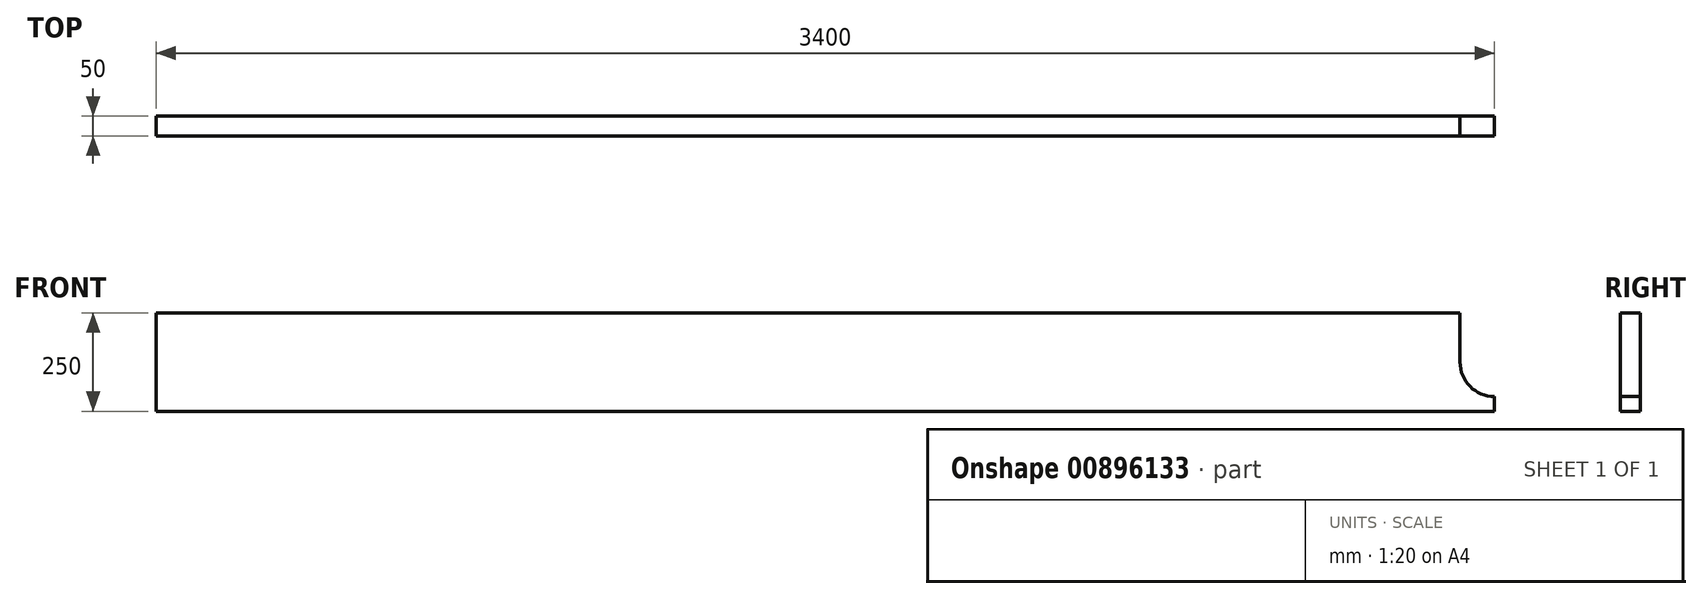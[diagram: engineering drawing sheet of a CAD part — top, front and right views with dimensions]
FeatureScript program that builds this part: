
annotation { "Feature Type Name" : "Feature", "Feature Type Description" : "" }
export const myFeature = defineFeature(function(context is Context, id is Id, definition is map)
    precondition{}
    {
        {
            var Q0;
            Q0=qCreatedBy(makeId("Front.planeOp"),FACE);
            var sketch = newSketch(context, id + "F0", { "sketchPlane" : qUnion([Q0])});
            skLineSegment(sketch, "E0.bottom", {"start": v(0, 0) * mm, "end": v(-3400, 0) * mm});
            skLineSegment(sketch, "E0.top", {"start": v(0, 250) * mm, "end": v(-3400, 250) * mm});
            skLineSegment(sketch, "E0.left", {"start": v(0, 0) * mm, "end": v(0, 250) * mm});
            skLineSegment(sketch, "E0.right", {"start": v(-3400, 0) * mm, "end": v(-3400, 250) * mm});
            skCircle(sketch, "E1", {"center": v(0, 125) * mm, "radius": 87.5 * mm});
            skLineSegment(sketch, "E2", {"start": v(-87.5, 250) * mm, "end": v(-87.5, 125) * mm});
            skSolve(sketch);
        }
        {
            var Q0;
            Q0=makeQuery(id+"F0.imprint","IMPRINT",FACE,{"disambiguationData":[TD([[makeQuery(id+"F0.imprint","IMPRINT",EDGE,{"derivedFrom":sQuery(id+"F0.wireOp",EDGE,"E0.bottom")}),-1.0]])]});
            extrude(context, id + "F1", {"entities" : qUnion([Q0]), "oppositeDirection" : true, "depth" : 50 * mm, "offsetDistance" : 25 * mm});
        }
        {
            var Q0;
            Q0=sQuery(id+"F0.wireOp",VERTEX,"E0.top.start");
            var Q1;
            Q1=makeQuery(id+"F1.opExtrude","SWEPT_BODY",BODY,{"disambiguationData":[OSD([sQuery(id+"F0.wireOp",EDGE,"E0.bottom"),sQuery(id+"F0.wireOp",EDGE,"E0.top"),sQuery(id+"F0.wireOp",EDGE,"E0.left"),sQuery(id+"F0.wireOp",EDGE,"E0.right")])]});
            hole(context, id + "F2", {"style" : HoleStyle.SIMPLE, "endStyle" : HoleEndStyle.THROUGH, "holeDiameter" : 175 * mm, "majorDiameter" : 5 * mm, "isTappedThrough" : true, "tappedDepth" : 12 * mm, "tapClearance" : 3, "locations" : qUnion([Q0]), "scope" : qUnion([Q1])});
        }
    });
